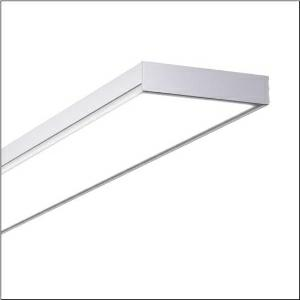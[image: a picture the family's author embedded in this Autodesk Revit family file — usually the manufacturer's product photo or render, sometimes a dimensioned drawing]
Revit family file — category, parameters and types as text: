
# Revit family: apollon_r__31_surface_51mp26wd2341e_c239
name_source: partatom
category: Lighting Fixtures
units: mm (PartAtom-declared; Revit-internal decimal feet)

## family parameters
Cut with Voids When Loaded = No
Host = Face
Light Source = No
Part Type = Normal
Room Calculation Point = No
Round Connector Dimension = Use Diameter
Shared = No

## types (1)
- Apollon® 31 Surface (1 x LED, 4400 lm, 33 W, 3000K)
    Apparent Load = 33 VA
    CIE Flux Codes = 61 87 97 97 100
    Color Rendering = 80
    Color Temperature = 3000K
    Default Elevation = 1800 mm
    Description = Apollon® 31 Surface, office luminaire, primary optical cover: micro prismatic cover, of PMMA, light emission: direct distribution, primary light characteristic: symmetric, installation type: surface-mounted, LED, rated luminous flux: 4.400lm, luminous efficacy: 133lm/W, light colour: 830, colour temperature: 3000K, control gear: DALI 2, with terminal, 5-pole, mains connection: 220..240V, AC, 50/60Hz, rated input power: 33W, housing, of sheet steel, coil coated, metallic grey (RAL 9006), length: 1.545mm, width: 200mm, height: 44mm, protection rating (complete): IP20, insulation class (complete): insulation class II (safety insulation), certification: CE, impact resistance: IK02, permissible operating ambient temperature: -20..+40°C, standard: EN 60598-2-22, packaging unit: 1 piece
    Height = 44 mm
    Lamp = 1 x LED
    Lamp Light Flux = 4400 lm
    Lamp Power = 33 W
    Lamp count = 1
    Length = 1545 mm
    Luminous efficacy = 133 lm/W
    Manufacturer = Siteco
    ModVariant = No
    Model = 51MP26WD2341E
    Mounting Place = Ceiling
    Mounting Type = Surface mounted
    Number of Poles = 1
    OnlyDefault = Yes
    Power Factor = 1
    Product Name = Apollon® 31 Surface
    Product group = office luminaire | ceiling mounted
    ProductGroupID = 303
    Protection Class = Protection class II
    Protection Degree = IP 20
    RLX_Detail_Level = 1
    RLX_Emergency_Light_Flux = 0 lm
    RLX_Emergency_Type = 0
    RLX_Emergency_Type_DB = No
    RlxData = <blob elided: 24093 chars, md5=9742f8d8>
    Socket = socket
    Standby Power = 0 W
    System Light Flux = 4400 lm
    System Power = 33 W
    Type Comments = Product without accessories
    Type Image = l_1313654.jpg
    URL = http://relux.com
    VarID = ---
    Voltage = 0 V
    Weight = 0.00 kg
    Width = 200 mm  [stored 0.656168 ft]

note: [stored X ft] marks values corroborated as IEEE doubles in the binary element streams (Revit-internal decimal feet)

## geometry (parser evidence)
native form markers: Blend x4, Sweep x10
no freeform markers — native parametric forms only
